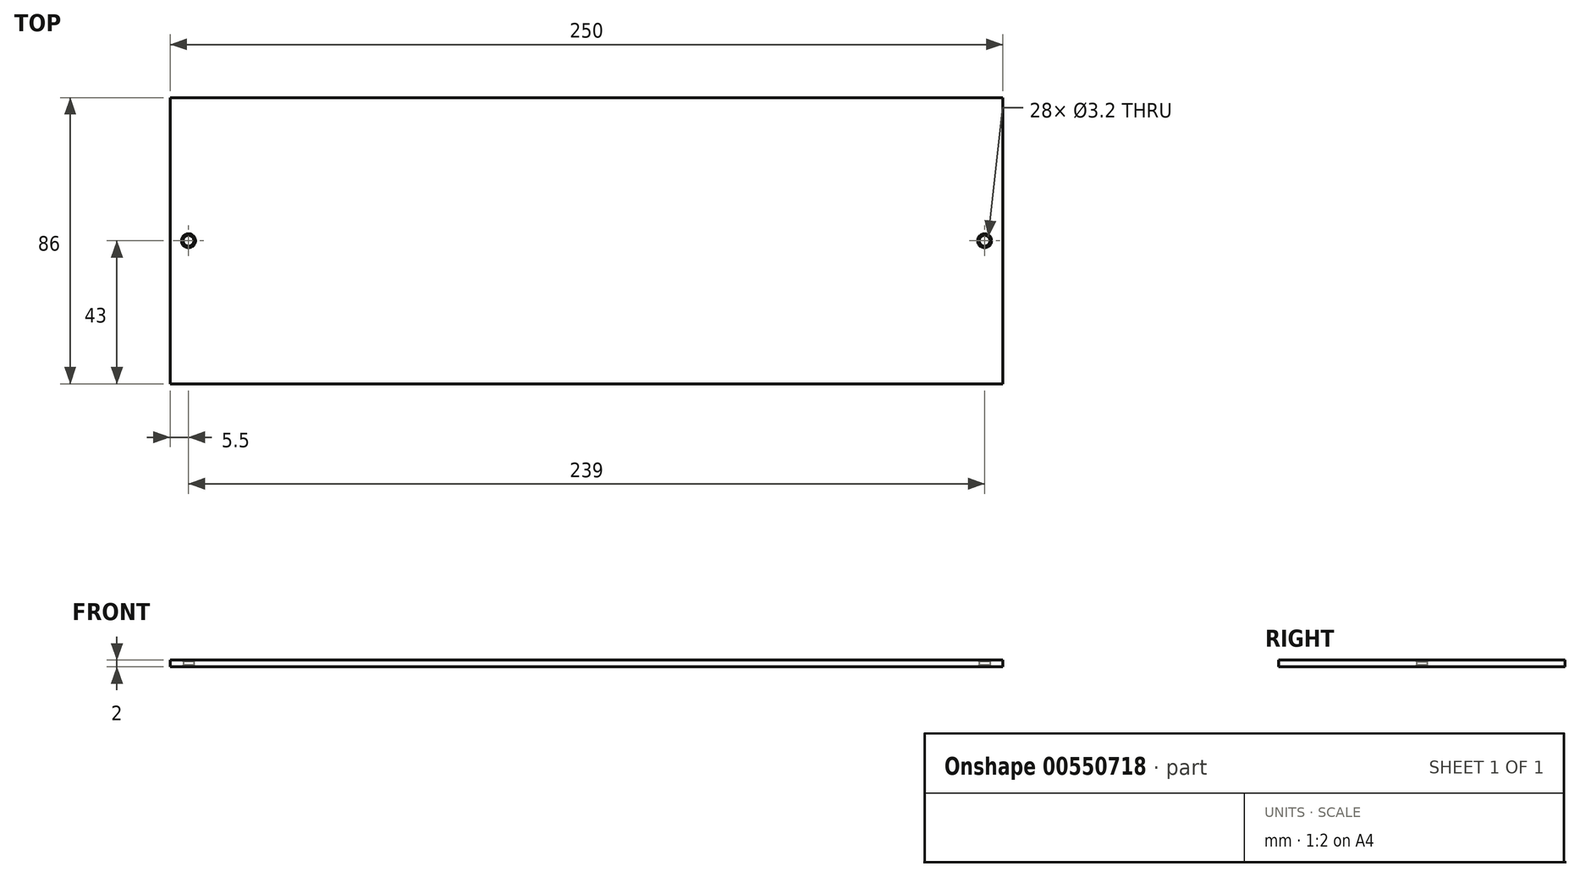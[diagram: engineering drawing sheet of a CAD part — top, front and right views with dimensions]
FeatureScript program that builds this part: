
annotation { "Feature Type Name" : "Feature", "Feature Type Description" : "" }
export const myFeature = defineFeature(function(context is Context, id is Id, definition is map)
    precondition{}
    {
        {
            var Q0;
            Q0=qCreatedBy(makeId("Top.planeOp"),FACE);
            var sketch = newSketch(context, id + "F0", { "sketchPlane" : qUnion([Q0])});
            skLineSegment(sketch, "E0.rect.bottom", {"start": v(-125, 43) * mm, "end": v(125, 43) * mm});
            skLineSegment(sketch, "E0.rect.top", {"start": v(-125, -43) * mm, "end": v(125, -43) * mm});
            skLineSegment(sketch, "E0.rect.left", {"start": v(-125, 43) * mm, "end": v(-125, -43) * mm});
            skLineSegment(sketch, "E0.rect.right", {"start": v(125, 43) * mm, "end": v(125, -43) * mm});
            skPoint(sketch, "E0.rect.middle", {"position": v(0, 0) * mm});
            skLineSegment(sketch, "E1", {"start": v(0, 43) * mm, "end": v(0, -43) * mm, "construction": true});
            skCircle(sketch, "E2", {"center": v(-119.5, 0) * mm, "radius": 1.6 * mm});
            skCircle(sketch, "E3.0.MirrorC", {"center": v(119.5, 0) * mm, "radius": 1.6 * mm});
            skSolve(sketch);
        }
        {
            var Q0;
            Q0=qSketchRegion(id+"F0",true);
            extrude(context, id + "F1", {"entities" : qUnion([Q0]), "depth" : 2 * mm});
        }
        {
            var Q0;
            Q0=makeQuery(id+"F1.opExtrude","SWEPT_FACE",FACE,{"disambiguationData":[OSD([sQuery(id+"F0.wireOp",EDGE,"E2")])]});
            var Q1;
            Q1=makeQuery(id+"F1.opExtrude","SWEPT_FACE",FACE,{"disambiguationData":[OSD([sQuery(id+"F0.wireOp",EDGE,"E3.0.MirrorC")])]});
            chamfer(context, id + "F2", {"entities" : qUnion([Q0, Q1]), "width" : 0.5 * mm, "tangentPropagation" : true});
        }
    });
